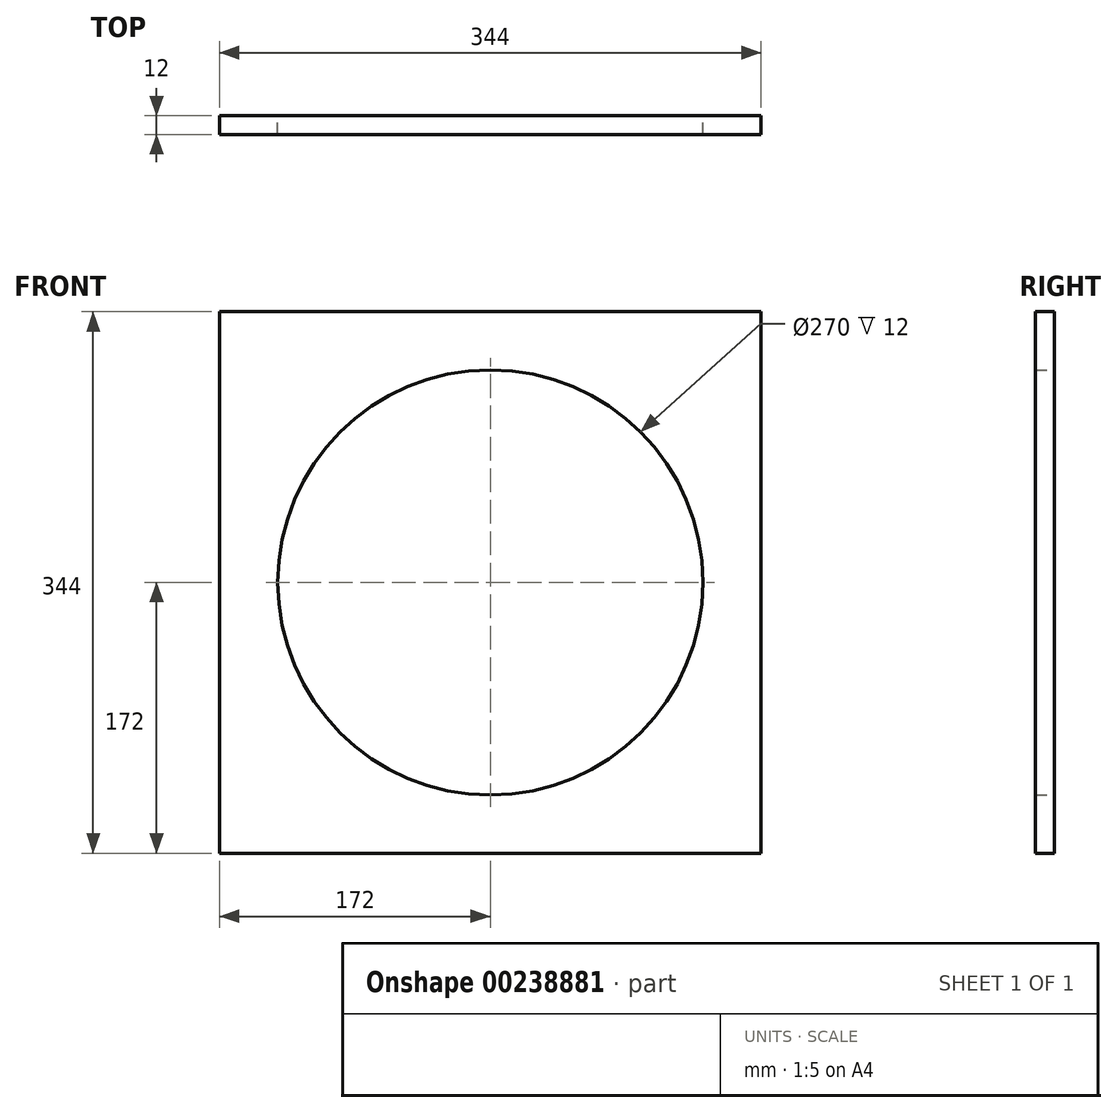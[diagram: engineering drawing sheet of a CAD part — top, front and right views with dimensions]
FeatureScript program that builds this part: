
annotation { "Feature Type Name" : "Feature", "Feature Type Description" : "" }
export const myFeature = defineFeature(function(context is Context, id is Id, definition is map)
    precondition{}
    {
        {
            var Q0;
            Q0=qCreatedBy(makeId("Front.planeOp"), FACE);
            var sketch = newSketch(context, id + "F0", { "sketchPlane" : qUnion([Q0])});
            skLineSegment(sketch, "E0.bottom", {"start": v(0, 0) * mm, "end": v(344, 0) * mm});
            skLineSegment(sketch, "E0.top", {"start": v(0, 344) * mm, "end": v(344, 344) * mm});
            skLineSegment(sketch, "E0.left", {"start": v(0, 0) * mm, "end": v(0, 344) * mm});
            skLineSegment(sketch, "E0.right", {"start": v(344, 0) * mm, "end": v(344, 344) * mm});
            skCircle(sketch, "E1", {"center": v(172, 172) * mm, "radius": 135 * mm});
            skSolve(sketch);
        }
        {
            var Q0;
            Q0 = qSketchRegion(id + "F0", true);
            extrude(context, id + "F1", {"entities" : qUnion([Q0]), "depth" : 12 * mm, "offsetDistance" : 25 * mm});
        }
    });
